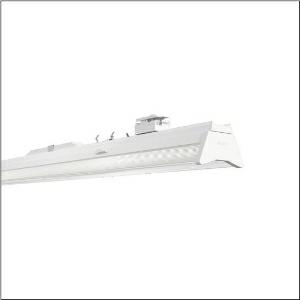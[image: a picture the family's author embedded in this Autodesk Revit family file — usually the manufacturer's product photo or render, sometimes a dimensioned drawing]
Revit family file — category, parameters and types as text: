
# Revit family: licross_r__11_performance_mo_51td16cn49xg_61c3
name_source: partatom
category: Lighting Fixtures
units: mm (PartAtom-declared; Revit-internal decimal feet)

## family parameters
Cut with Voids When Loaded = No
Host = Face
Light Source = No
Part Type = Normal
Room Calculation Point = No
Round Connector Dimension = Use Diameter
Shared = No

## types (1)
- --- (1 x LED, 9190 lm, 49.4 W, 4000K)
    Apparent Load = 49 VA
    CIE Flux Codes = 66 88 96 79 100
    Color Rendering = 80
    Color Temperature = 4000K
    Default Elevation = 1800 mm
    Description = Licross® 11 Performance MO, luminaire insert, of sheet steel, galvanised, coil coated, white, length: 1.500mm, width: 120mm, height: 123mm, LED rated luminous flux: 9.190lm, light colour: 840, control gear: ON/OFF Multilumen, CLOi, with plug, 3-pole, with phase selection, mains connection: 220..240V, AC, 50/60Hz, start of lifetime: 49W, end of service life: 55W, internal wiring halogen-free, primary light control with lens, of plastic, primary optical cover: cover, of PMMA, light emission: direct/indirect distribution, primary light characteristic: symmetric, protection rating (complete): IP54, insulation class (complete): insulation class I (protective earthing), certification: CE, ENEC, VDE, UKCA, protection symbol: D if used in an environment with non-conductive dust loads with corresponding accessories, impact resistance: IK06, permissible ambient temperature for indoor applications: -35..+40°C, corresponds to IFS (International Featured Standards) requirements for safety and quality in the food industry, reducing of maximum allowable ambient temperature of 5°C with ceiling mounting, LABS conformity tested according to VDMA 24364:2018-05, packaging unit: 1 piece
    Height = 114 mm
    Lamp = 1 x LED
    Lamp Light Flux = 9190 lm
    Lamp Power = 49.4 W
    Lamp count = 1
    Length = 1500 mm
    Luminous efficacy = 186 lm/W
    Manufacturer = Siteco
    ModVariant = No
    Model = 51TD16CN49XG
    Mounting Place = Ceiling
    Mounting Type = Pendant
    Number of Poles = 1
    OnlyDefault = Yes
    Power Factor = 1
    Product Name = Licross® 11 Performance MO
    Product group = luminaire insert | ceiling pendant
    ProductGroupID = 902
    Protection Class = Protection class I
    Protection Degree = IP 54
    RLX_Detail_Level = 1
    RLX_Emergency_Light_Flux = 0 lm
    RLX_Emergency_Type = 0
    RLX_Emergency_Type_DB = No
    RlxData = <blob elided: 31865 chars, md5=d0e5a5eb>
    Socket = socket
    Standby Power = 0 W
    System Light Flux = 9190 lm
    System Power = 49 W
    Type Comments = factory setting: luminous flux: 100 % | (A | C | E) | 113 mA
    Type Image = l_1256138.jpg
    URL = http://relux.com
    VarID = @adj_107587
    Voltage = 0 V
    Weight = 0.00 kg
    Width = 120 mm

## geometry (parser evidence)
native form markers: Blend x4, Sweep x10
no freeform markers — native parametric forms only
